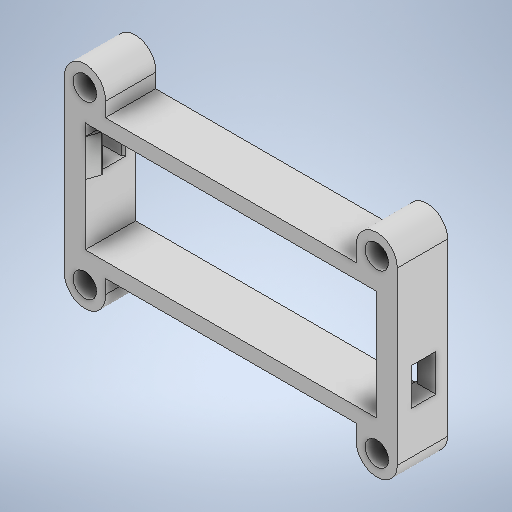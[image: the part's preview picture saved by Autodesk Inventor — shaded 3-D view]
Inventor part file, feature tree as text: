
AUTODESK INVENTOR PART (.ipt)
format: ipt  version: 2025.1 (Build 291241000, 241)  size: 344,576 bytes
history: native  units: mm
features: extrude x6, sketch x6, chamfer x4, plane x1
ambient origin geometry x8: Origin, YZ Plane, XZ Plane, XY Plane, X Axis, Y Axis, Z Axis, Center Point
bodies: Solid1 (feature_tree)
feature tree (17):
  extrude  "Extrusion1"  Depth=26.2mm
  sketch  "Sketch2"  dims[d2=3.5mm d3=3.5mm]
  sketch  "Sketch3"  dims[d4=69.5mm d5=12.0mm d6=0.0mm]
  extrude  "Extrusion2"  Depth=3.5mm
  extrude  "Extrusion3"  Depth=12.0mm TaperAngle=0.0deg
  extrude  "Extrusion4"  Depth=2.8mm
  extrude  "Extrusion5"  Depth=8.85mm
  chamfer  "Chamfer1"  Distance=2.8mm
  extrude  "Extrusion6"  Depth=5.8mm
  chamfer  "Chamfer2"  Distance=8.85mm
  chamfer  "Chamfer3"  Distance=12.0mm
  chamfer  "Chamfer4"  Distance=10.0mm
  plane  "Work Plane1"
  sketch  "Sketch1"  dims[d0=5.0mm d1=26.2mm]
  sketch  "Sketch4"  dims[d7=2.8mm d8=2.8mm]
  sketch  "Sketch5"  dims[d9=5.8mm d10=8.85mm]
  sketch  "Sketch6"  dims[d11=2.8mm d12=2.8mm d13=5.8mm d14=8.85mm d15=12.0mm d16=0.0mm d17=10.0mm d18=0.0mm d19=4.9mm d20=5.6mm d21=3.8mm d22=10.0mm d23=0.0mm d24=1.2mm d25=0.0mm d26=3.4mm d27=1.2mm d28=45.0deg d29=1.2mm d30=0.0mm d31=3.4mm d32=1.2mm d33=45.0deg d34=0.5mm d35=1.2mm d36=45.0deg d37=0.5mm d38=1.2mm d39=45.0deg]
